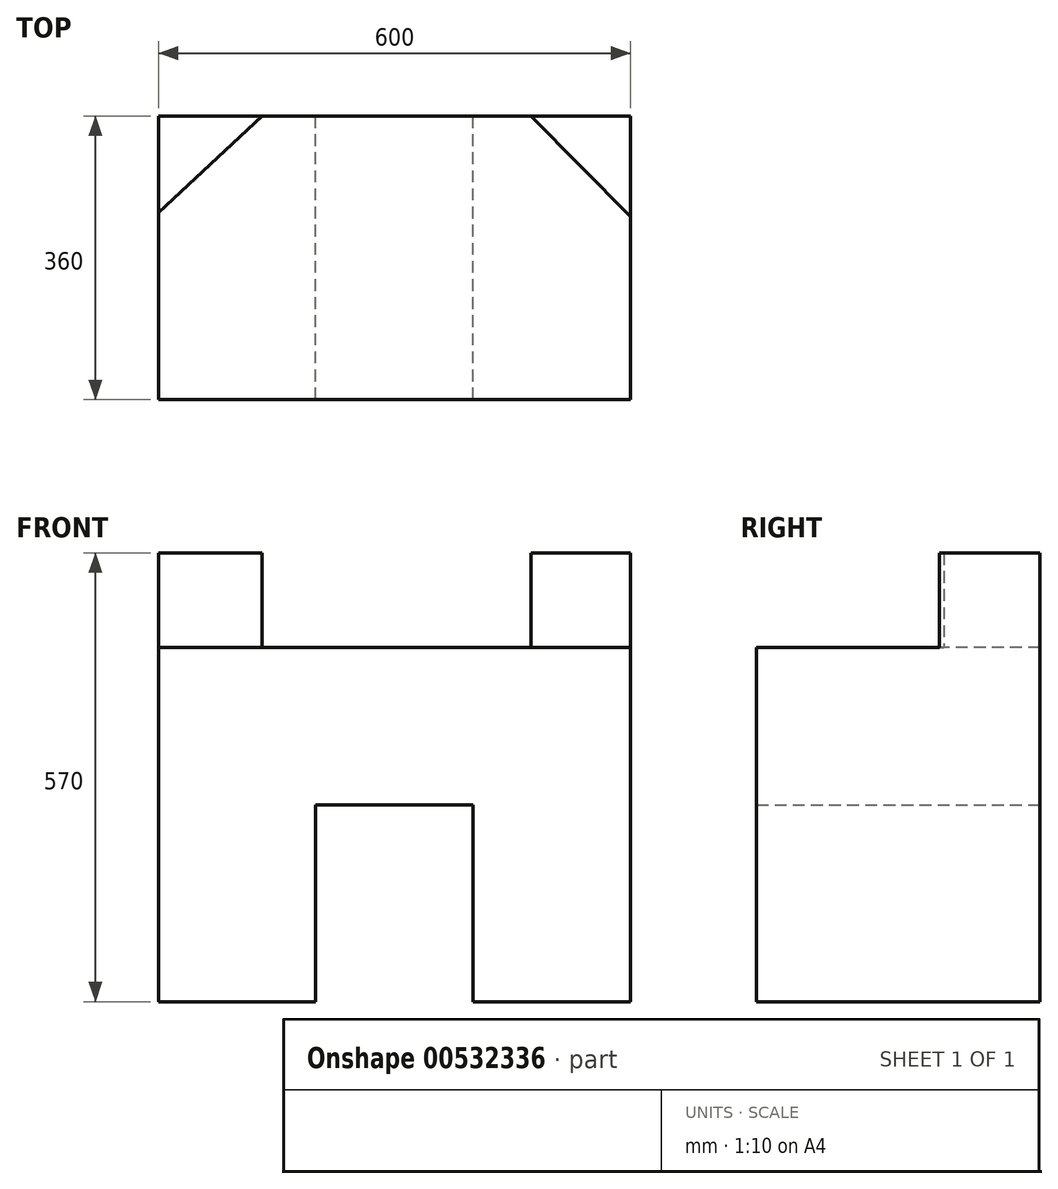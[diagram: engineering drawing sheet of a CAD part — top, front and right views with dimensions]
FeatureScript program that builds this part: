
annotation { "Feature Type Name" : "Feature", "Feature Type Description" : "" }
export const myFeature = defineFeature(function(context is Context, id is Id, definition is map)
    precondition{}
    {
        {
            var Q0;
            Q0=qCreatedBy(makeId("Front.planeOp"),FACE);
            var sketch = newSketch(context, id + "F0", { "sketchPlane" : qUnion([Q0])});
            skLineSegment(sketch, "E0.bottom", {"start": v(-300, -225) * mm, "end": v(300, -225) * mm});
            skLineSegment(sketch, "E0.top", {"start": v(-300, 225) * mm, "end": v(300, 225) * mm});
            skLineSegment(sketch, "E0.left", {"start": v(-300, -225) * mm, "end": v(-300, 225) * mm});
            skLineSegment(sketch, "E0.right", {"start": v(300, -225) * mm, "end": v(300, 225) * mm});
            skPoint(sketch, "E0.middle", {"position": v(0, 0) * mm});
            skLineSegment(sketch, "E1", {"start": v(-300, -225) * mm, "end": v(-100, -225) * mm});
            skLineSegment(sketch, "E2", {"start": v(-100, -225) * mm, "end": v(-100, 25) * mm});
            skLineSegment(sketch, "E3", {"start": v(-100, 25) * mm, "end": v(100, 25) * mm});
            skLineSegment(sketch, "E4", {"start": v(100, 25) * mm, "end": v(100, -225) * mm});
            skLineSegment(sketch, "E5", {"start": v(100, -225) * mm, "end": v(300, -225) * mm});
            skSolve(sketch);
        }
        {
            var Q0;
            Q0=makeQuery(id+"F0.imprint","IMPRINT",FACE,{"disambiguationData":[TD([[makeQuery(id+"F0.imprint","IMPRINT",EDGE,{"derivedFrom":sQuery(id+"F0.wireOp",EDGE,"E0.top")}),-1.0]])]});
            extrude(context, id + "F1", {"entities" : qUnion([Q0]), "depth" : 360 * mm, "offsetDistance" : 25 * mm});
        }
        {
            var Q0;
            Q0=makeQuery(id+"F1.opExtrude","SWEPT_FACE",FACE,{"disambiguationData":[OSD([sQuery(id+"F0.wireOp",EDGE,"E0.top")])]});
            var sketch = newSketch(context, id + "F2", { "sketchPlane" : qUnion([Q0])});
            skLineSegment(sketch, "E6", {"start": v(-167.97, 0) * mm, "end": v(-300, -122.35) * mm});
            skLineSegment(sketch, "E7", {"start": v(173.33, 0) * mm, "end": v(300, -127.89) * mm});
            skSolve(sketch);
        }
        {
            var Q0;
            Q0 = qSketchRegion(id + "F2", true);
            var Q1;
            {var subQ0=sQuery(id+"F2.wireOp",EDGE,"E6");Q1=makeQuery(id+"F2.imprint","IMPRINT",FACE,{"disambiguationData":[TD([[makeQuery(id+"F2.imprint","IMPRINT",EDGE,{"derivedFrom":subQ0}),-1.0]])]});}
            var Q2;
            {var subQ0=sQuery(id+"F2.wireOp",EDGE,"E7");Q2=makeQuery(id+"F2.imprint","IMPRINT",FACE,{"disambiguationData":[TD([[makeQuery(id+"F2.imprint","IMPRINT",EDGE,{"derivedFrom":subQ0}),1.0]])]});}
            extrude(context, id + "F3", {"entities" : qUnion([Q0, Q1, Q2]), "operationType" : NewBodyOperationType.ADD, "depth" : 120 * mm, "offsetDistance" : 25 * mm});
        }
    });
